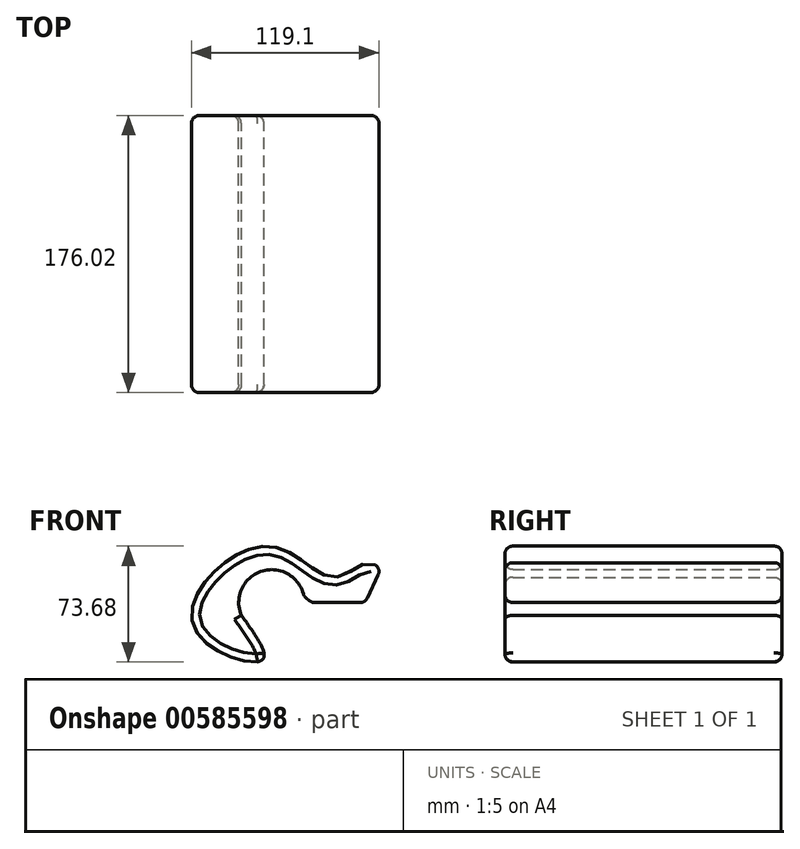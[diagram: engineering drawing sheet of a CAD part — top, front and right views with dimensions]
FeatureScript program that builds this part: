
annotation { "Feature Type Name" : "Feature", "Feature Type Description" : "" }
export const myFeature = defineFeature(function(context is Context, id is Id, definition is map)
    precondition{}
    {
        {
            var Q0;
            Q0=qCreatedBy(makeId("Front.planeOp"),FACE);
            var sketch = newSketch(context, id + "F0", { "sketchPlane" : qUnion([Q0])});
            skLineSegment(sketch, "E0.bottom", {"start": v(-24.36, -22.42) * mm, "end": v(40.06, -22.42) * mm});
            skLineSegment(sketch, "E0.top", {"start": v(-24.36, 24.87) * mm, "end": v(40.06, 24.87) * mm});
            skLineSegment(sketch, "E0.left", {"start": v(-24.36, -22.42) * mm, "end": v(-24.36, 24.87) * mm});
            skLineSegment(sketch, "E0.right", {"start": v(40.06, -22.42) * mm, "end": v(40.06, 24.87) * mm});
            skArc(sketch, "E1", {"start": v(-24.36, 24.87) * mm, "mid": v(-49.43, 45.36) * mm, "end": v(-64.52, 16.72) * mm});
            skFitSpline(sketch, "E2", {"points": [v(-64.52, 16.72) * mm, v(-51.88, -12.03) * mm, v(-95.5, 11.62) * mm, v(-49.03, 60.75) * mm, v(-6.42, 40.97) * mm, v(17.43, 50.15) * mm, v(40.06, 24.87) * mm, v(67.58, 6.52) * mm, v(40.06, -22.42) * mm, v(12.74, -34.04) * mm, v(-24.36, -22.42) * mm], "startDerivative": vector(309.18, -424.4) * mm, "endDerivative": vector(-396.34, 173.17) * mm});
            skSolve(sketch);
        }
        {
            var Q0;
            {var subQ0=sQuery(id+"F0.wireOp",EDGE,"E0.top");Q0=makeQuery(id+"F0.imprint","IMPRINT",FACE,{"disambiguationData":[TD([[makeQuery(id+"F0.imprint","IMPRINT",EDGE,{"derivedFrom":subQ0}),1.0]])]});}
            extrude(context, id + "F1", {"entities" : qUnion([Q0]), "depth" : 150.62 * mm, "offsetDistance" : 25.4 * mm, "hasSecondDirection" : true, "secondDirectionOppositeDirection" : true, "secondDirectionDepth" : 25.4 * mm});
        }
        {
            var Q0;
            Q0=makeQuery(id+"F1.opExtrude","SWEPT_EDGE",EDGE,{"disambiguationData":[OSD([sQuery(id+"F0.wireOp",EDGE,"E0.top"),sQuery(id+"F0.wireOp",EDGE,"E0.right"),sQuery(id+"F0.wireOp",EDGE,"E2")])]});
            chamfer(context, id + "F2", {"entities" : qUnion([Q0]), "width" : 12.7 * mm, "tangentPropagation" : true});
        }
        {
            var Q0;
            Q0=makeQuery(id+"F1.opExtrude","SWEPT_EDGE",EDGE,{"disambiguationData":[OSD([sQuery(id+"F0.wireOp",EDGE,"E0.top"),sQuery(id+"F0.wireOp",EDGE,"E0.left"),sQuery(id+"F0.wireOp",EDGE,"E1")])]});
            chamfer(context, id + "F3", {"entities" : qUnion([Q0]), "width" : 5.08 * mm, "tangentPropagation" : true});
        }
        {
            var Q0;
            {var subQ0=sQuery(id+"F0.wireOp",EDGE,"E2");Q0=makeQuery(id+"F2.opChamfer","BLEND_EDGE",EDGE,{"blendedFrom":[makeQuery(id+"F1.opExtrude","SWEPT_EDGE",EDGE,{"disambiguationData":[OSD([sQuery(id+"F0.wireOp",EDGE,"E0.top"),sQuery(id+"F0.wireOp",EDGE,"E0.right"),subQ0])]}),makeQuery(id+"F1.opExtrude","SWEPT_FACE",FACE,{"disambiguationData":[OSD([subQ0])]})],"blendedInto":[makeQuery(id+"F1.opExtrude","SWEPT_FACE",FACE,{"disambiguationData":[OSD([subQ0])]})]});}
            fillet(context, id + "F4", {"entities" : qUnion([Q0]), "radius" : 5.08 * mm, "tangentPropagation" : true, "allowEdgeOverflow" : false});
        }
        {
            var Q0;
            {var subQ0=sQuery(id+"F0.wireOp",EDGE,"E0.top");Q0=makeQuery(id+"F2.opChamfer","BLEND_EDGE",EDGE,{"blendedFrom":[makeQuery(id+"F1.opExtrude","SWEPT_EDGE",EDGE,{"disambiguationData":[OSD([subQ0,sQuery(id+"F0.wireOp",EDGE,"E0.right"),sQuery(id+"F0.wireOp",EDGE,"E2")])]}),makeQuery(id+"F1.opExtrude","SWEPT_FACE",FACE,{"disambiguationData":[OSD([subQ0])]})],"blendedInto":[makeQuery(id+"F1.opExtrude","SWEPT_FACE",FACE,{"disambiguationData":[OSD([subQ0])]})]});}
            fillet(context, id + "F5", {"entities" : qUnion([Q0]), "radius" : 5.08 * mm, "tangentPropagation" : true, "allowEdgeOverflow" : false});
        }
        {
            var Q0;
            {var subQ0=sQuery(id+"F0.wireOp",EDGE,"E0.top");Q0=makeQuery(id+"F3.opChamfer","BLEND_EDGE",EDGE,{"blendedFrom":[makeQuery(id+"F1.opExtrude","SWEPT_EDGE",EDGE,{"disambiguationData":[OSD([subQ0,sQuery(id+"F0.wireOp",EDGE,"E0.left"),sQuery(id+"F0.wireOp",EDGE,"E1")])]}),makeQuery(id+"F1.opExtrude","SWEPT_FACE",FACE,{"disambiguationData":[OSD([subQ0])]})],"blendedInto":[makeQuery(id+"F1.opExtrude","SWEPT_FACE",FACE,{"disambiguationData":[OSD([subQ0])]})]});}
            fillet(context, id + "F6", {"entities" : qUnion([Q0]), "radius" : 5.08 * mm, "tangentPropagation" : true, "allowEdgeOverflow" : false});
        }
        {
            var Q0;
            {var subQ0=sQuery(id+"F0.wireOp",EDGE,"E1");Q0=makeQuery(id+"F3.opChamfer","BLEND_EDGE",EDGE,{"blendedFrom":[makeQuery(id+"F1.opExtrude","SWEPT_EDGE",EDGE,{"disambiguationData":[OSD([sQuery(id+"F0.wireOp",EDGE,"E0.top"),sQuery(id+"F0.wireOp",EDGE,"E0.left"),subQ0])]}),makeQuery(id+"F1.opExtrude","SWEPT_FACE",FACE,{"disambiguationData":[OSD([subQ0])]})],"blendedInto":[makeQuery(id+"F1.opExtrude","SWEPT_FACE",FACE,{"disambiguationData":[OSD([subQ0])]})]});}
            fillet(context, id + "F7", {"entities" : qUnion([Q0]), "radius" : 5.08 * mm, "tangentPropagation" : true, "allowEdgeOverflow" : false});
        }
        {
            var Q0;
            Q0=makeQuery(id+"F1.opExtrude","CAP_EDGE",EDGE,{"disambiguationData":[OSD([sQuery(id+"F0.wireOp",EDGE,"E0.top")])],"isStart":true});
            fillet(context, id + "F8", {"entities" : qUnion([Q0]), "radius" : 5.08 * mm, "tangentPropagation" : true, "allowEdgeOverflow" : false});
        }
        {
            var Q0;
            Q0=makeQuery(id+"F1.opExtrude","CAP_EDGE",EDGE,{"disambiguationData":[OSD([sQuery(id+"F0.wireOp",EDGE,"E0.top")])],"isStart":false});
            fillet(context, id + "F9", {"entities" : qUnion([Q0]), "radius" : 5.08 * mm, "tangentPropagation" : true, "allowEdgeOverflow" : false});
        }
    });
